# Revit family: 117-38
name_source: partatom
category: Plumbing Fixtures
revit_build: Autodesk Revit 2015 (Build: 20140223_1515(x64)
units: mm (PartAtom-declared; Revit-internal decimal feet)

## types (1)
- 117-38
    CW Connection = Yes
    Certification = http://www.helvex.com.mx
    Chrome = Brass Chromed
    Compliance = NOM-005-CONAGUA-1996
    Connection = 1" Feeding Connection
    Description = Oscilating Handle Flush Valve For WC Special Straight Nipple Of 23.62"  For 1.50" Diameter Top Spud
    Documentation = http://www.helvex.com.mx
    Features = Lever With Antibacterial Coating; Left Or Right Connection
    Flow = 6.0 Lts Per Flush
    Manufacturer = HELVEX
    Max. Working Pressure = 85.3 psi
    Min. Working Pressure = 14.2 psi
    Model = 117-38
    Note = Feeding Pipe Must Be 1 ¼" And Connect 1 ¼" - 1" Reductor to Stop Valve
    Type Comments = Flush Valves
    URL = http://www.helvex.com.mx

## geometry (parser evidence)
native form markers: Sweep x2
no freeform markers — native parametric forms only
